# Revit family: FU_Table_Sandler_Momo 2
name_source: partatom
category: Furniture
units: mm (PartAtom-declared; Revit-internal decimal feet)

## family parameters
Always vertical = Yes
Cut with Voids When Loaded = No
OmniClass Number = 23.40.20.00
OmniClass Title = General Furniture and Specialties
Room Calculation Point = No
Shared = No
Work Plane-Based = No

## types (2) — shared parameters
Height = 1050 mm
Manufacturer = Sandler
URL = https://www.sandlerseating.com
zero-valued in all types: Default Elevation

## per-type parameters (varying)
| type | Description | Frame | Top | Top Type |
| MOMO TABLE 2-600 | Bar height table base with 60cm / 24″ diameter folding top. The base is in steel treated with cataphoresis process. | Metal - Powdercoat - Dark Grey NCS 7500-N | Metal - Powdercoat - Dark Grey NCS 7500-N | FU_Table Top_Ta : 600mm Rnd Top |
| MOMO TABLE 2Q-600 | Bar height table base with 60cm x 60cm / 24″ x 24″ folding top. The base is in steel treated with cataphoresis process. | Metal - Powdercoat - Dark Green NCS 8010-G10Y | Metal - Powdercoat - Dark Green NCS 8010-G10Y | FU_Table Top_Ta-Q : 600mm Sqr Top |

note: column(s) folded — value = type name in every type: Model

## geometry (parser evidence)
native form markers: Sweep x9
no freeform markers — native parametric forms only
